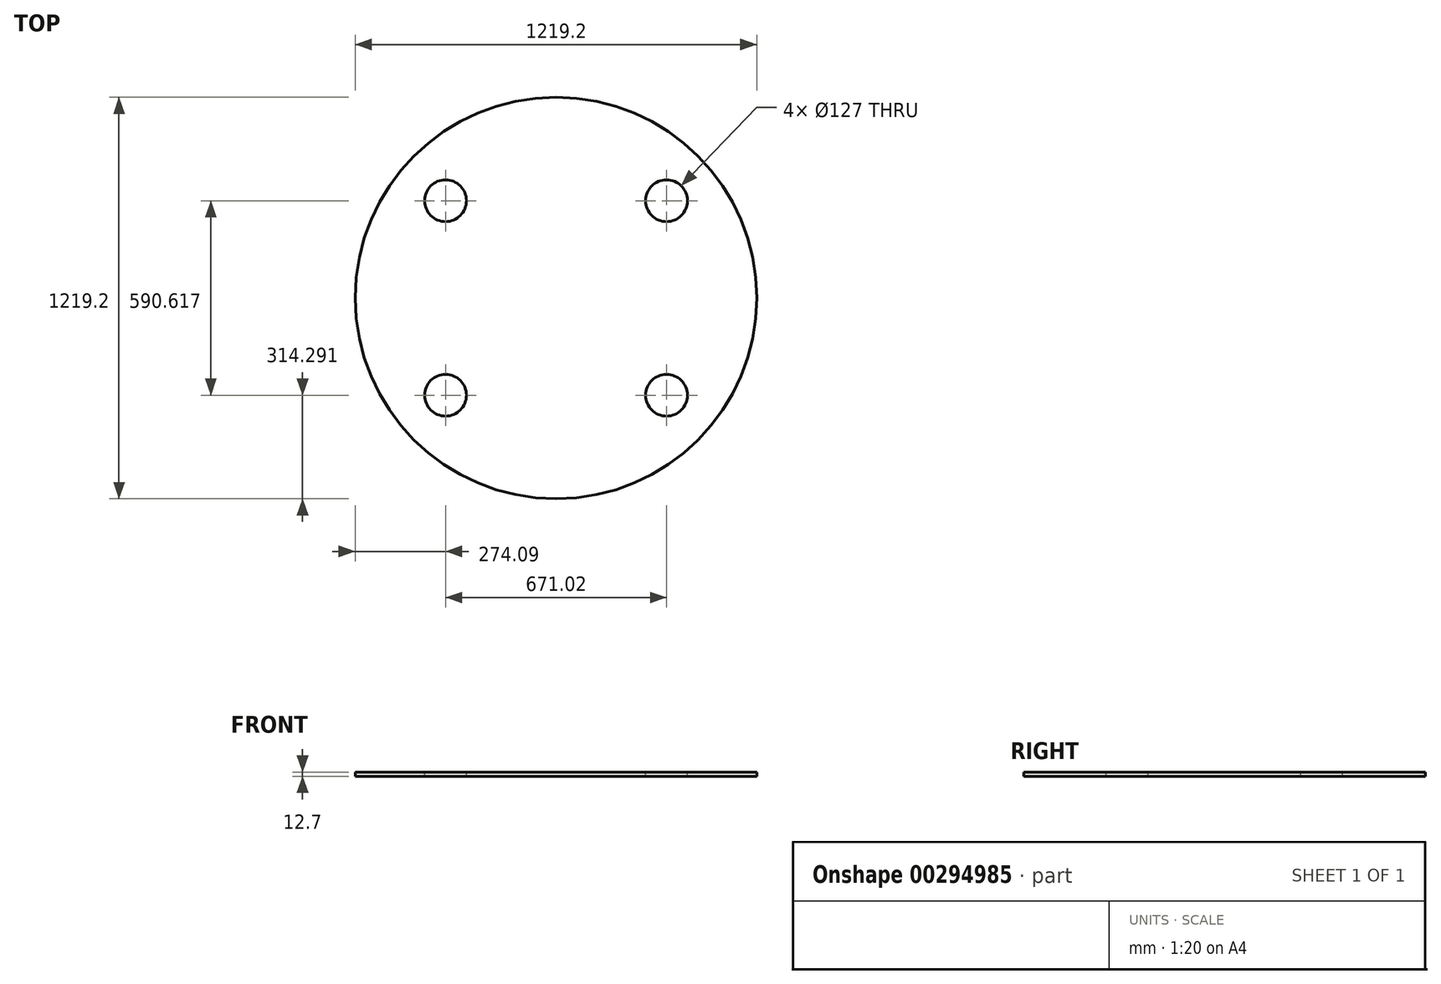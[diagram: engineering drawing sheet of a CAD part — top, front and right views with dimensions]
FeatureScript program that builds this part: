
annotation { "Feature Type Name" : "Feature", "Feature Type Description" : "" }
export const myFeature = defineFeature(function(context is Context, id is Id, definition is map)
    precondition{}
    {
        {
            var Q0;
            Q0=qCreatedBy(makeId("Top.planeOp"),FACE);
            var sketch = newSketch(context, id + "F0", { "sketchPlane" : qUnion([Q0])});
            skCircle(sketch, "E0", {"center": v(0, 0) * mm, "radius": 609.6 * mm});
            skSolve(sketch);
        }
        {
            var Q0;
            Q0 = qSketchRegion(id + "F0", true);
            extrude(context, id + "F1", {"entities" : qUnion([Q0]), "depth" : 12.7 * mm});
        }
        {
            var Q0;
            Q0=makeQuery(id+"F1.opExtrude","CAP_FACE",FACE,{"disambiguationData":[OSD([sQuery(id+"F0.wireOp",EDGE,"E0")])],"isStart":false});
            var sketch = newSketch(context, id + "F2", { "sketchPlane" : qUnion([Q0])});
            skLineSegment(sketch, "E1", {"start": v(609.6, 0) * mm, "end": v(-609.6, 0) * mm});
            skLineSegment(sketch, "E2", {"start": v(0, 609.6) * mm, "end": v(0, -609.6) * mm});
            skCircle(sketch, "E3", {"center": v(335.5, -295.3) * mm, "radius": 63.5 * mm});
            skCircle(sketch, "E4.MirrorC", {"center": v(335.5, 295.3) * mm, "radius": 63.5 * mm});
            skCircle(sketch, "E5.MirrorC", {"center": v(-335.5, 295.3) * mm, "radius": 63.5 * mm});
            skCircle(sketch, "E6.MirrorC", {"center": v(-335.5, -295.3) * mm, "radius": 63.5 * mm});
            skSolve(sketch);
        }
        {
            var Q0;
            Q0=sQuery(id+"F2.wireOp",VERTEX,"E4.MirrorC.center");
            var Q1;
            Q1=sQuery(id+"F2.wireOp",VERTEX,"E3.center");
            var Q2;
            Q2=sQuery(id+"F2.wireOp",VERTEX,"E6.MirrorC.center");
            var Q3;
            Q3=sQuery(id+"F2.wireOp",VERTEX,"E5.MirrorC.center");
            var Q4;
            Q4=makeQuery(id+"F1.opExtrude","SWEPT_BODY",BODY,{"disambiguationData":[OSD([sQuery(id+"F0.wireOp",EDGE,"E0")])]});
            hole(context, id + "F3", {"style" : HoleStyle.SIMPLE, "endStyle" : HoleEndStyle.THROUGH, "holeDiameter" : 127 * mm, "tappedDepth" : 12.7 * mm, "tapClearance" : 3, "locations" : qUnion([Q0, Q1, Q2, Q3]), "scope" : qUnion([Q4])});
        }
    });
